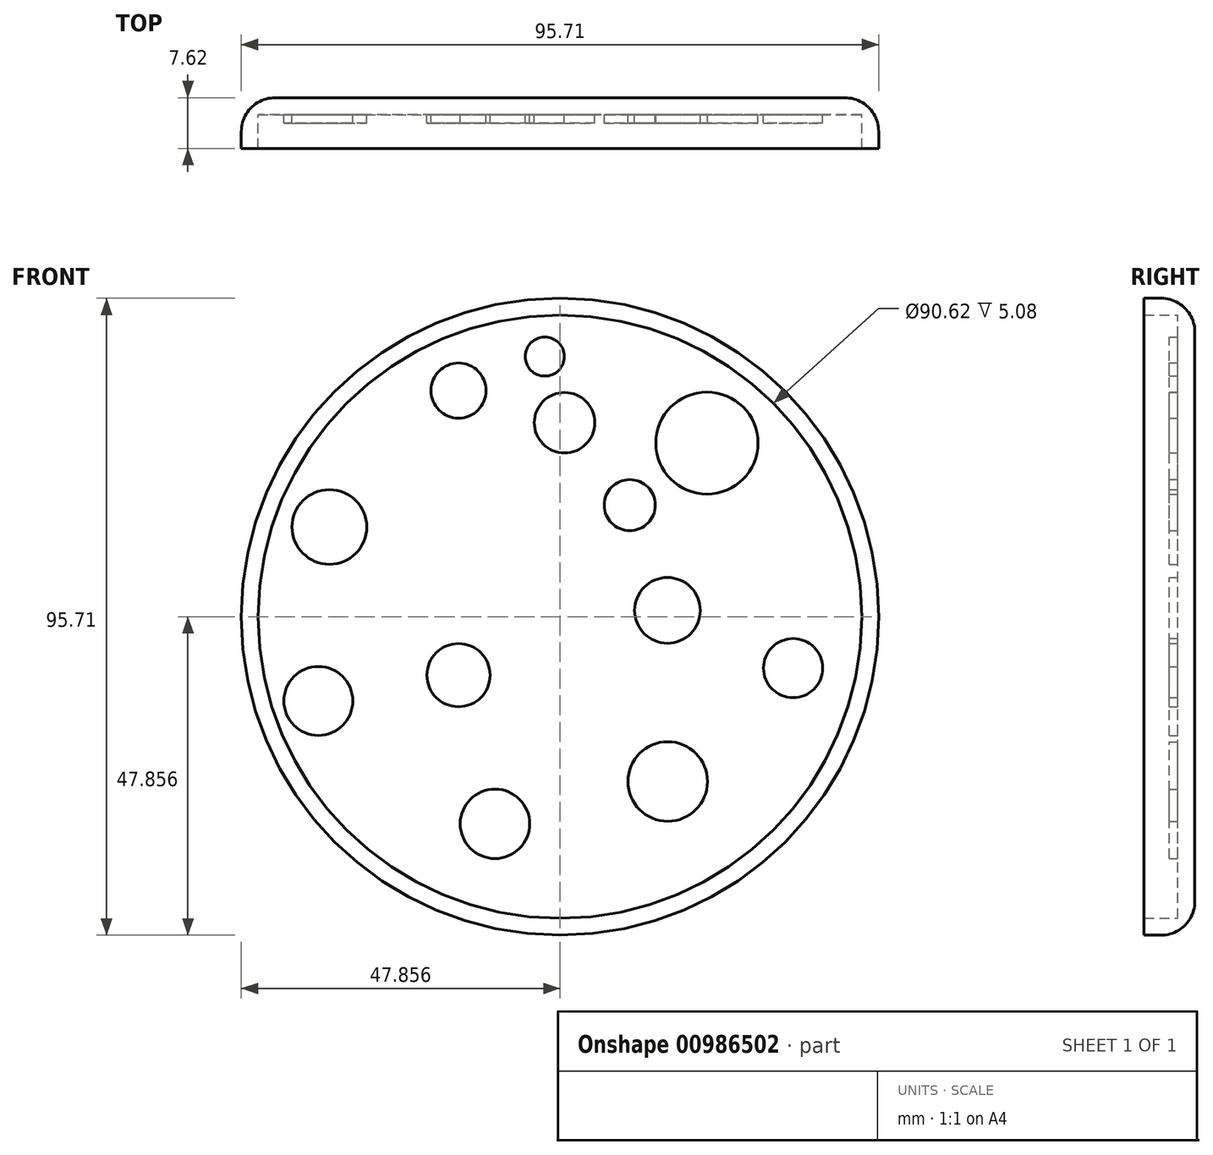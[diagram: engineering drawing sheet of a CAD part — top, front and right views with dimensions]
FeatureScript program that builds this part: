
annotation { "Feature Type Name" : "Feature", "Feature Type Description" : "" }
export const myFeature = defineFeature(function(context is Context, id is Id, definition is map)
    precondition{}
    {
        {
            var Q0;
            Q0=qCreatedBy(makeId("Front.planeOp"),FACE);
            var sketch = newSketch(context, id + "F0", { "sketchPlane" : qUnion([Q0])});
            skCircle(sketch, "E0", {"center": v(-75.71, 36.77) * mm, "radius": 47.85 * mm});
            skSolve(sketch);
        }
        {
            var Q0;
            Q0=makeQuery(id+"F0.imprint","IMPRINT",FACE,{"disambiguationData":[TD([[makeQuery(id+"F0.imprint","IMPRINT",EDGE,{"derivedFrom":sQuery(id+"F0.wireOp",EDGE,"E0")}),1.0]])]});
            extrude(context, id + "F1", {"entities" : qUnion([Q0]), "depth" : 7.62 * mm, "offsetDistance" : 25.4 * mm});
        }
        {
            var Q0;
            Q0=makeQuery(id+"F1.opExtrude","CAP_FACE",FACE,{"disambiguationData":[OSD([sQuery(id+"F0.wireOp",EDGE,"E0")])],"isStart":false});
            shell(context, id + "F2", {"entities" : qUnion([Q0]), "thickness" : 2.54 * mm});
        }
        {
            var Q0;
            {var subQ0=sQuery(id+"F0.wireOp",EDGE,"E0");Q0=makeQuery(id+"F2.opShell","OFFSET_FACE",FACE,{"disambiguationData":[OSD([subQ0]),TDD([makeQuery(id+"F1.opExtrude","CAP_FACE",FACE,{"disambiguationData":[OSD([subQ0])],"isStart":true})])]});}
            var sketch = newSketch(context, id + "F3", { "sketchPlane" : qUnion([Q0])});
            skLineSegment(sketch, "E1", {"start": v(-112, 63.9) * mm, "end": v(-39.02, 10.18) * mm});
            skLineSegment(sketch, "E2", {"start": v(-97.12, -3.17) * mm, "end": v(-59.98, 79.26) * mm});
            skLineSegment(sketch, "E3", {"start": v(-87.72, 80.46) * mm, "end": v(-67.97, -7.88) * mm});
            skLineSegment(sketch, "E4", {"start": v(-119.97, 27.06) * mm, "end": v(-32.47, 50.29) * mm});
            skSolve(sketch);
        }
        {
            var Q0;
            {var subQ0=sQuery(id+"F3.wireOp",EDGE,"E4");var subQ4=sQuery(id+"F3.wireOp",EDGE,"E2");var subQ5=makeQuery(id+"F3.imprint","INTERSECT",VERTEX,{"derivedFrom":[subQ4,subQ0]});Q0=makeQuery(id+"F3.imprint","IMPRINT",FACE,{"disambiguationData":[TD([[makeQuery(id+"F3.imprint","IMPRINT",EDGE,{"disambiguationData":[TD([[subQ5,-1.0]])],"derivedFrom":subQ4}),1.0]])]});}
            var sketch = newSketch(context, id + "F4", { "sketchPlane" : qUnion([Q0])});
            skCircle(sketch, "E5", {"center": v(-110.34, 50.25) * mm, "radius": 5.6 * mm});
            skCircle(sketch, "E6", {"center": v(-112, 24.1) * mm, "radius": 5.18 * mm});
            skCircle(sketch, "E7", {"center": v(-85.48, 5.65) * mm, "radius": 5.22 * mm});
            skCircle(sketch, "E8", {"center": v(-59.54, 12) * mm, "radius": 5.98 * mm});
            skCircle(sketch, "E9", {"center": v(-59.58, 37.71) * mm, "radius": 4.94 * mm});
            skCircle(sketch, "E10", {"center": v(-40.7, 29.04) * mm, "radius": 4.45 * mm});
            skCircle(sketch, "E11", {"center": v(-90.95, 27.98) * mm, "radius": 4.75 * mm});
            skCircle(sketch, "E12", {"center": v(-90.95, 70.74) * mm, "radius": 4.14 * mm});
            skCircle(sketch, "E13", {"center": v(-77.99, 75.85) * mm, "radius": 2.94 * mm});
            skCircle(sketch, "E14", {"center": v(-75.02, 65.91) * mm, "radius": 4.54 * mm});
            skCircle(sketch, "E15", {"center": v(-53.65, 62.85) * mm, "radius": 7.67 * mm});
            skCircle(sketch, "E16", {"center": v(-65.23, 53.53) * mm, "radius": 3.84 * mm});
            skSolve(sketch);
        }
        {
            var Q0;
            Q0 = qSketchRegion(id + "F4", true);
            extrude(context, id + "F5", {"entities" : qUnion([Q0]), "operationType" : NewBodyOperationType.ADD, "depth" : 1.27 * mm, "offsetDistance" : 25.4 * mm});
        }
        {
            var Q0;
            Q0=makeQuery(id+"F1.opExtrude","CAP_EDGE",EDGE,{"disambiguationData":[OSD([sQuery(id+"F0.wireOp",EDGE,"E0")])],"isStart":true});
            fillet(context, id + "F6", {"entities" : qUnion([Q0]), "radius" : 5.08 * mm, "tangentPropagation" : true, "allowEdgeOverflow" : false});
        }
    });
